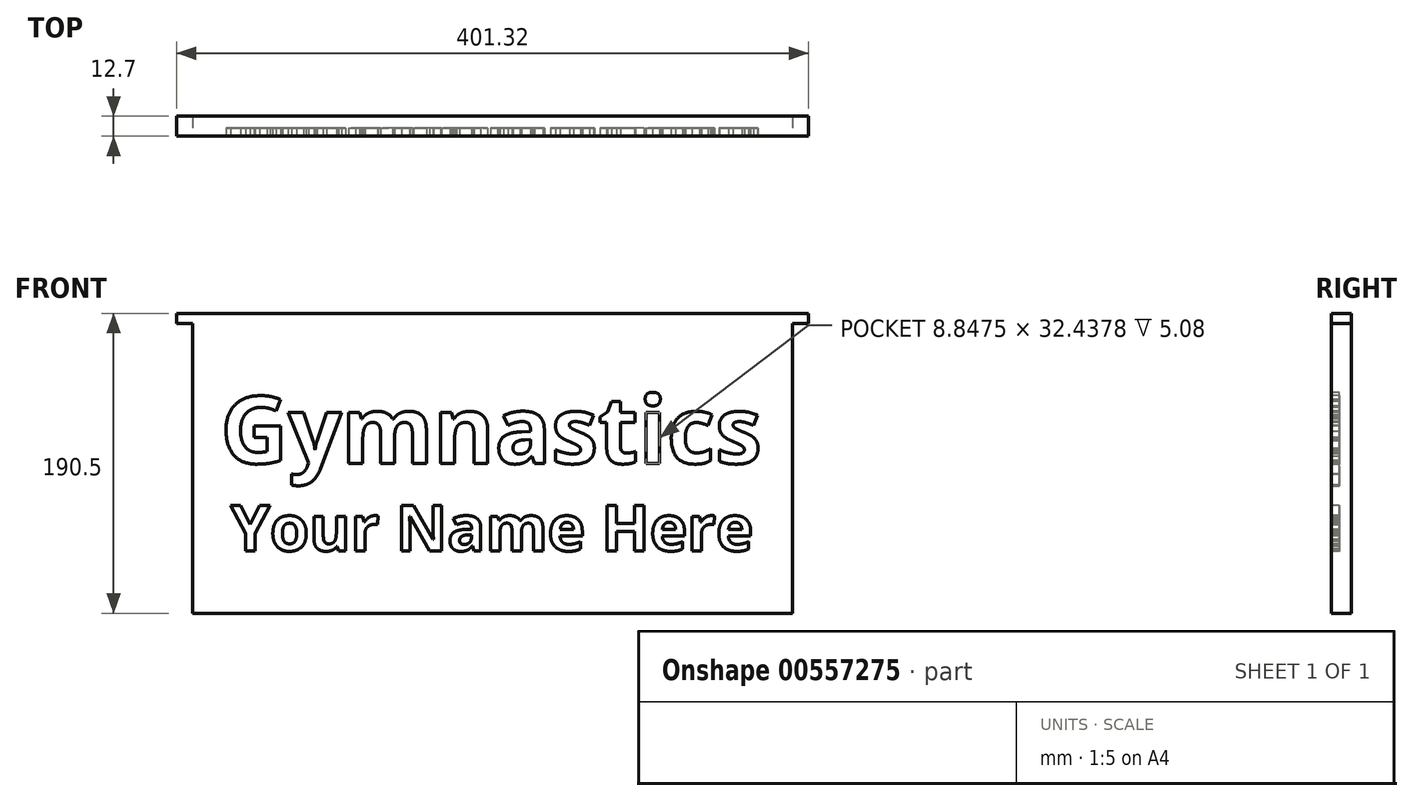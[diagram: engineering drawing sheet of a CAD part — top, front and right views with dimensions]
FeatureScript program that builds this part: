
annotation { "Feature Type Name" : "Feature", "Feature Type Description" : "" }
export const myFeature = defineFeature(function(context is Context, id is Id, definition is map)
    precondition{}
    {
        {
            var Q0;
            Q0=qCreatedBy(makeId("Front.planeOp"),FACE);
            var sketch = newSketch(context, id + "F0", { "sketchPlane" : qUnion([Q0])});
            skLineSegment(sketch, "E0.bottom", {"start": v(-200.66, 95.25) * mm, "end": v(200.66, 95.25) * mm});
            skLineSegment(sketch, "E0.top", {"start": v(-200.66, -95.25) * mm, "end": v(200.66, -95.25) * mm});
            skLineSegment(sketch, "E0.left", {"start": v(-200.66, 95.25) * mm, "end": v(-200.66, -95.25) * mm});
            skLineSegment(sketch, "E0.right", {"start": v(200.66, 95.25) * mm, "end": v(200.66, -95.25) * mm});
            skPoint(sketch, "E0.middle", {"position": v(0, 0) * mm});
            skSolve(sketch);
        }
        {
            var Q0;
            Q0=makeQuery(id+"F0.imprint","IMPRINT",FACE,{"disambiguationData":[TD([[makeQuery(id+"F0.imprint","IMPRINT",EDGE,{"derivedFrom":sQuery(id+"F0.wireOp",EDGE,"E0.bottom")}),-1.0]])]});
            extrude(context, id + "F1", {"entities" : qUnion([Q0]), "depth" : 12.7 * mm});
        }
        {
            var Q0;
            Q0=makeQuery(id+"F1.opExtrude","CAP_FACE",FACE,{"disambiguationData":[OSD([sQuery(id+"F0.wireOp",EDGE,"E0.bottom"),sQuery(id+"F0.wireOp",EDGE,"E0.top"),sQuery(id+"F0.wireOp",EDGE,"E0.left"),sQuery(id+"F0.wireOp",EDGE,"E0.right")])],"isStart":false});
            var sketch = newSketch(context, id + "F2", { "sketchPlane" : qUnion([Q0])});
            skText(sketch, "E1", { "text": "Gymnastics", "fontName": "OpenSans-Bold.ttf"});
            skText(sketch, "E2", { "text": "Your Name Here", "fontName": "OpenSans-Bold.ttf"});
            const initialGuessF2  = {"E1": [-0.17278, 0, 1, 0, 0.04278], "E2": [-0.16647, -0.05555, 1, 0, 0.02893]};
            skSetInitialGuess(sketch, initialGuessF2);
            skSolve(sketch);
        }
        {
            var Q0;
            Q0=qSketchRegion(id+"F2",true);
            extrude(context, id + "F3", {"entities" : qUnion([Q0]), "operationType" : NewBodyOperationType.REMOVE, "oppositeDirection" : true, "depth" : 5.08 * mm});
        }
        {
            var Q0;
            {var subQ0=sQuery(id+"F0.wireOp",EDGE,"E0.left");var subQ1=sQuery(id+"F0.wireOp",EDGE,"E0.bottom");var subQ2=sQuery(id+"F0.wireOp",EDGE,"E0.right");var subQ3=sQuery(id+"F0.wireOp",EDGE,"E0.top");Q0=makeQuery(id+"F3.boolean.opBoolean","SPLIT",FACE,{"disambiguationData":[TD([makeQuery(id+"F1.opExtrude","SWEPT_FACE",FACE,{"disambiguationData":[OSD([subQ1])]})])],"derivedFrom":makeQuery(id+"F1.opExtrude","CAP_FACE",FACE,{"disambiguationData":[OSD([subQ1,subQ3,subQ0,subQ2])],"isStart":false})});}
            var sketch = newSketch(context, id + "F4", { "sketchPlane" : qUnion([Q0])});
            skPoint(sketch, "E3", {"position": v(-190.5, 95.25) * mm});
            skPoint(sketch, "E4", {"position": v(-190.5, -95.25) * mm});
            skPoint(sketch, "E5", {"position": v(190.5, 95.25) * mm});
            skPoint(sketch, "E6", {"position": v(200.66, 88.9) * mm});
            skPoint(sketch, "E7", {"position": v(190.5, -95.25) * mm});
            skPoint(sketch, "E8", {"position": v(-200.66, 88.9) * mm});
            skLineSegment(sketch, "E9", {"start": v(-190.5, 95.25) * mm, "end": v(-190.5, -95.25) * mm});
            skLineSegment(sketch, "E10", {"start": v(-200.66, 88.9) * mm, "end": v(-190.5, 88.9) * mm});
            skLineSegment(sketch, "E11", {"start": v(190.5, -95.25) * mm, "end": v(190.5, 95.25) * mm});
            skLineSegment(sketch, "E12", {"start": v(200.66, 88.9) * mm, "end": v(190.5, 88.9) * mm});
            skPoint(sketch, "E13", {"position": v(-32.37, -40.44) * mm});
            skPoint(sketch, "E14", {"position": v(-37.84, -40.44) * mm});
            skSolve(sketch);
        }
        {
            var Q0;
            {var subQ3=sQuery(id+"F4.wireOp",EDGE,"E10");Q0=makeQuery(id+"F4.imprint","IMPRINT",FACE,{"disambiguationData":[TD([[makeQuery(id+"F4.imprint","IMPRINT",EDGE,{"derivedFrom":subQ3}),-1.0]])]});}
            var Q1;
            {var subQ3=sQuery(id+"F4.wireOp",EDGE,"E12");Q1=makeQuery(id+"F4.imprint","IMPRINT",FACE,{"disambiguationData":[TD([[makeQuery(id+"F4.imprint","IMPRINT",EDGE,{"derivedFrom":subQ3}),1.0]])]});}
            extrude(context, id + "F5", {"entities" : qUnion([Q0, Q1]), "operationType" : NewBodyOperationType.REMOVE, "oppositeDirection" : true, "depth" : 12.7 * mm});
        }
    });
